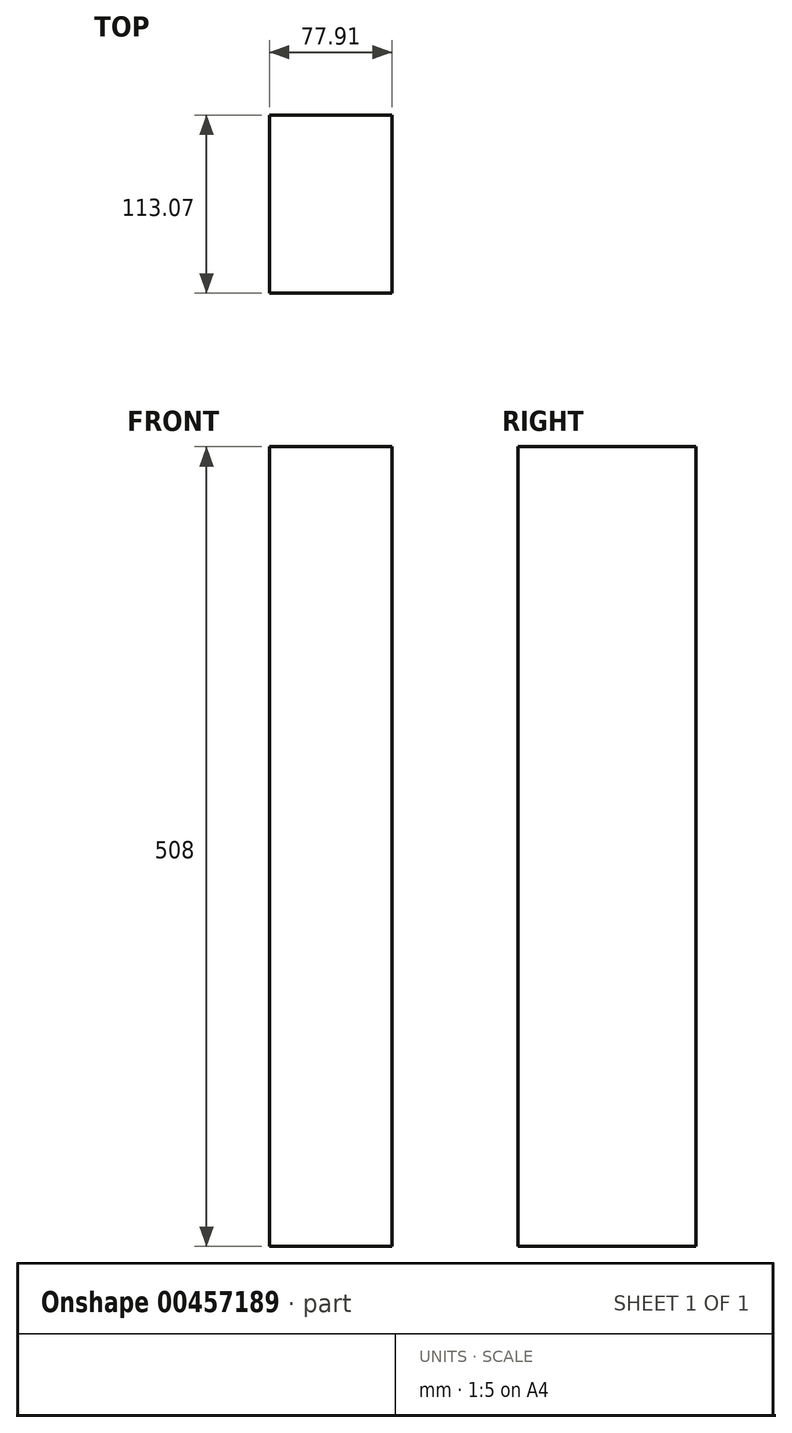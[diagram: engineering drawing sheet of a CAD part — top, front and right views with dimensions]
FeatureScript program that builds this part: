
annotation { "Feature Type Name" : "Feature", "Feature Type Description" : "" }
export const myFeature = defineFeature(function(context is Context, id is Id, definition is map)
    precondition{}
    {
        {
            var Q0;
            Q0=qCreatedBy(makeId("Top.planeOp"),FACE);
            var sketch = newSketch(context, id + "F0", { "sketchPlane" : qUnion([Q0])});
            skLineSegment(sketch, "E0.bottom", {"start": v(-43.63, 34.6) * mm, "end": v(-46.37, 34.6) * mm});
            skLineSegment(sketch, "E0.top", {"start": v(-43.63, 29.97) * mm, "end": v(-46.37, 29.97) * mm});
            skLineSegment(sketch, "E0.left", {"start": v(-43.63, 34.6) * mm, "end": v(-43.63, 29.97) * mm});
            skLineSegment(sketch, "E0.right", {"start": v(-46.37, 34.6) * mm, "end": v(-46.37, 29.97) * mm});
            skLineSegment(sketch, "E1.bottom", {"start": v(34.28, 49.63) * mm, "end": v(-43.63, 49.63) * mm});
            skLineSegment(sketch, "E1.top", {"start": v(34.28, -63.44) * mm, "end": v(-43.63, -63.44) * mm});
            skLineSegment(sketch, "E1.left", {"start": v(34.28, 49.63) * mm, "end": v(34.28, -63.44) * mm});
            skLineSegment(sketch, "E1.right", {"start": v(-43.63, 49.63) * mm, "end": v(-43.63, -63.44) * mm});
            skSolve(sketch);
        }
        {
            var Q0;
            {var subQ2=sQuery(id+"F0.wireOp",EDGE,"E1.bottom");Q0=makeQuery(id+"F0.imprint","IMPRINT",FACE,{"disambiguationData":[TD([[makeQuery(id+"F0.imprint","IMPRINT",EDGE,{"derivedFrom":subQ2}),1.0]])]});}
            extrude(context, id + "F1", {"entities" : qUnion([Q0]), "endBound" : BoundingType.SYMMETRIC, "depth" : 508 * mm});
        }
    });
